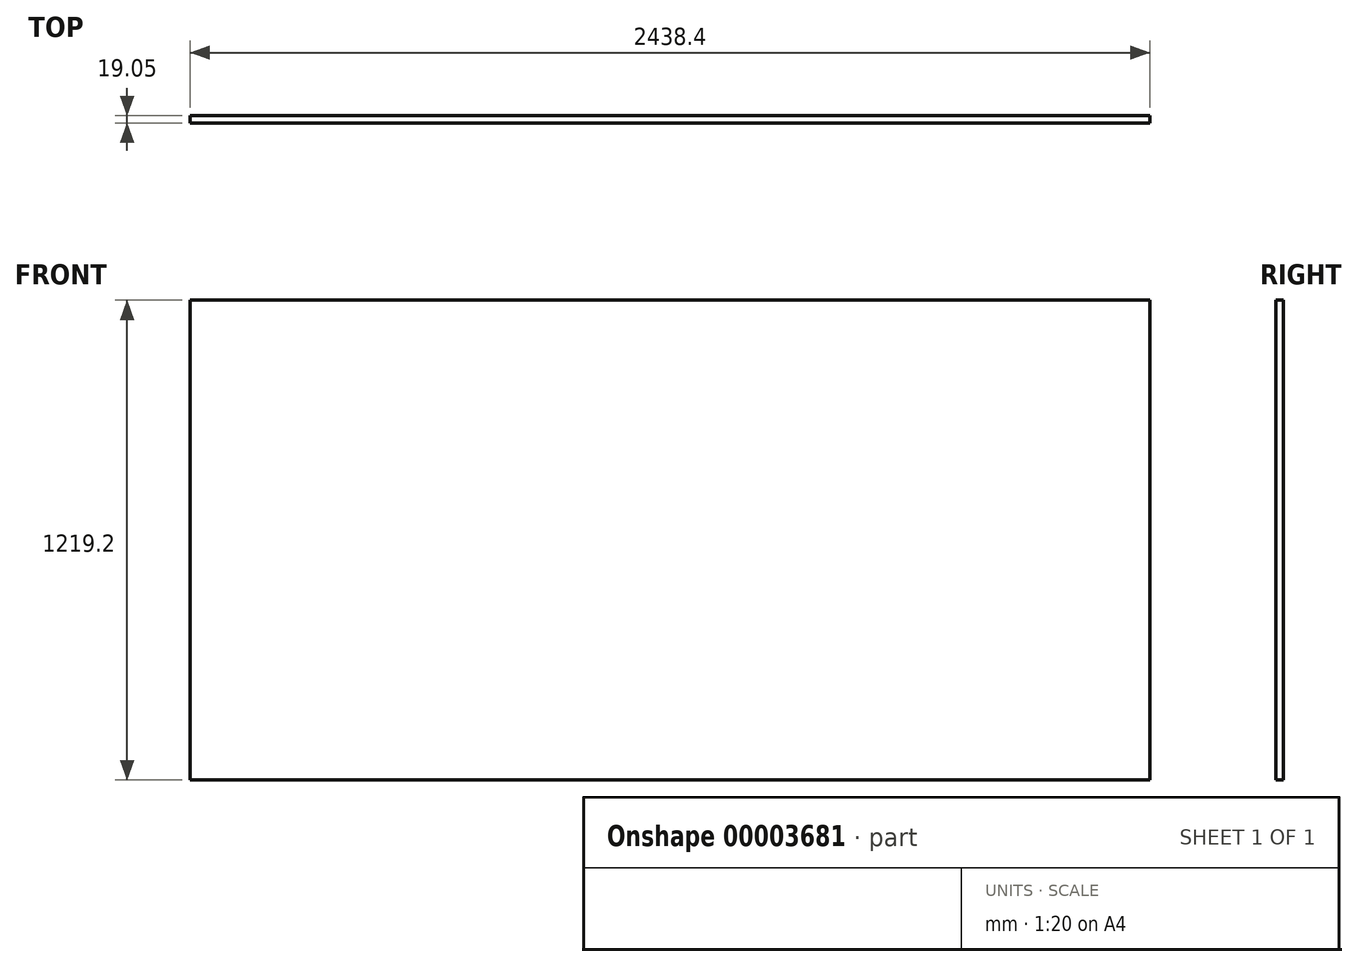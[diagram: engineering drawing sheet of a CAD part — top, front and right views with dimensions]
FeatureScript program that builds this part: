
annotation { "Feature Type Name" : "Feature", "Feature Type Description" : "" }
export const myFeature = defineFeature(function(context is Context, id is Id, definition is map)
    precondition{}
    {
        {
            var Q0;
            Q0=qCreatedBy(makeId("Front.planeOp"),FACE);
            var sketch = newSketch(context, id + "F0", { "sketchPlane" : qUnion([Q0])});
            skLineSegment(sketch, "E0.bottom", {"start": v(0, 0) * mm, "end": v(2438.4, 0) * mm});
            skLineSegment(sketch, "E0.top", {"start": v(0, 1219.2) * mm, "end": v(2438.4, 1219.2) * mm});
            skLineSegment(sketch, "E0.left", {"start": v(0, 0) * mm, "end": v(0, 1219.2) * mm});
            skLineSegment(sketch, "E0.right", {"start": v(2438.4, 0) * mm, "end": v(2438.4, 1219.2) * mm});
            skSolve(sketch);
        }
        {
            var Q0;
            Q0=makeQuery(id+"F0.imprint","IMPRINT",FACE,{"disambiguationData":[TD([[makeQuery(id+"F0.imprint","IMPRINT",EDGE,{"derivedFrom":sQuery(id+"F0.wireOp",EDGE,"E0.bottom")}),1.0]])]});
            extrude(context, id + "F1", {"entities" : qUnion([Q0]), "depth" : 19.05 * mm});
        }
    });
